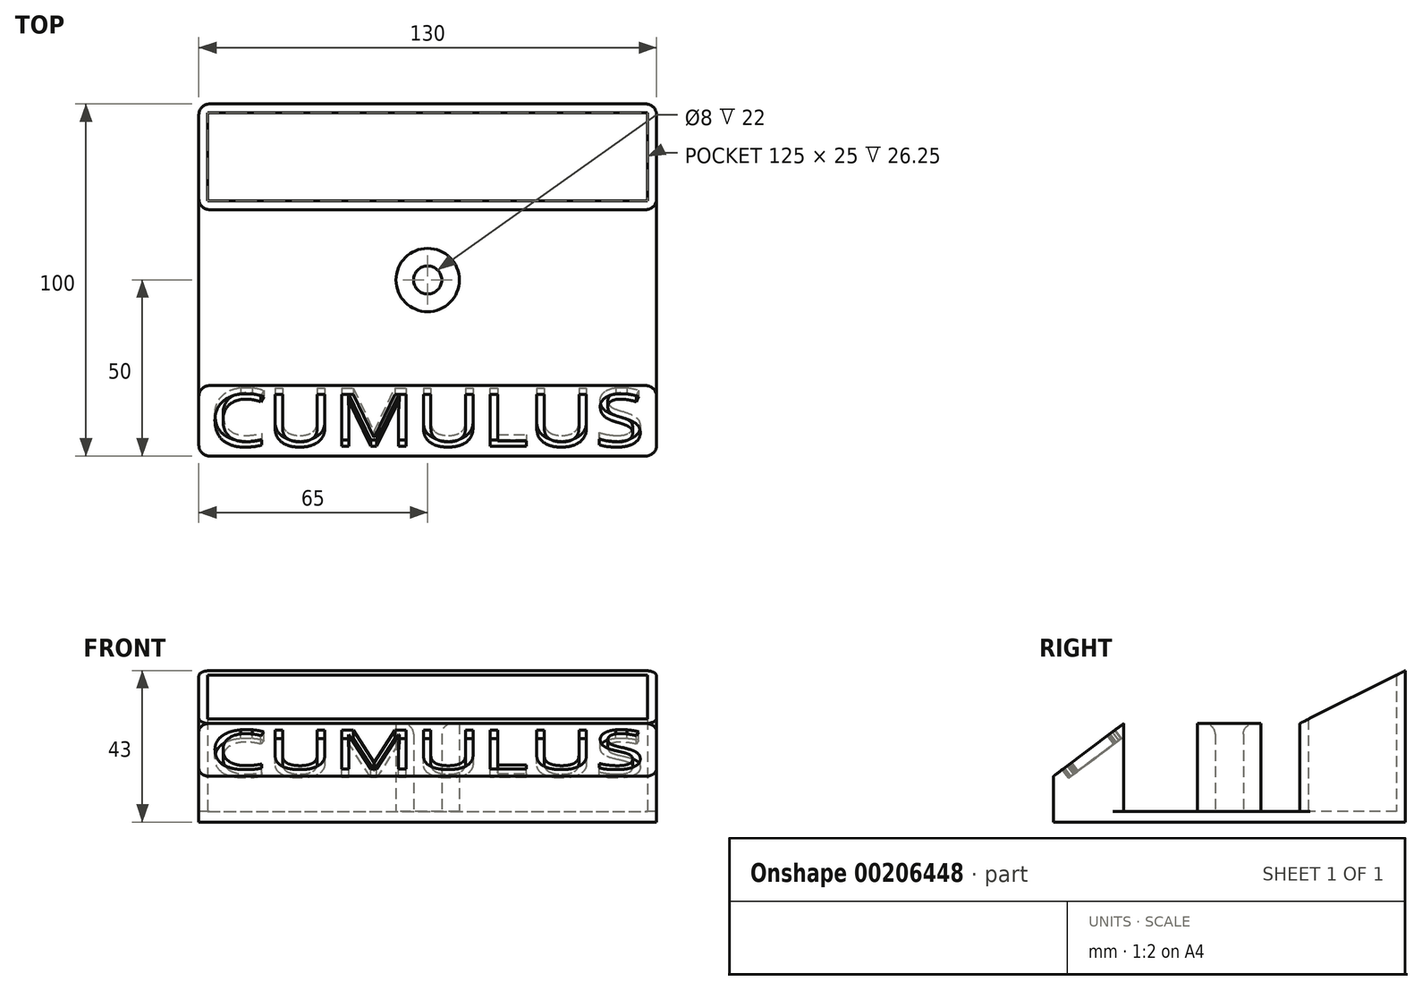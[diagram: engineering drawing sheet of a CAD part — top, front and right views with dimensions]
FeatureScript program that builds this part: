
annotation { "Feature Type Name" : "Feature", "Feature Type Description" : "" }
export const myFeature = defineFeature(function(context is Context, id is Id, definition is map)
    precondition{}
    {
        {
            var Q0;
            Q0=qCreatedBy(makeId("Top.planeOp"),FACE);
            var sketch = newSketch(context, id + "F0", { "sketchPlane" : qUnion([Q0])});
            skLineSegment(sketch, "E0.bottom", {"start": v(-65, 100) * mm, "end": v(65, 100) * mm});
            skLineSegment(sketch, "E0.top", {"start": v(-65, 0) * mm, "end": v(65, 0) * mm});
            skLineSegment(sketch, "E0.left", {"start": v(65, 100) * mm, "end": v(65, 0) * mm});
            skLineSegment(sketch, "E0.right", {"start": v(-65, 100) * mm, "end": v(-65, 0) * mm});
            skSolve(sketch);
        }
        {
            var Q0;
            Q0=makeQuery(id+"F0.imprint","IMPRINT",FACE,{"disambiguationData":[TD([[makeQuery(id+"F0.imprint","IMPRINT",EDGE,{"derivedFrom":sQuery(id+"F0.wireOp",EDGE,"E0.bottom")}),-1.0]])]});
            extrude(context, id + "F1", {"entities" : qUnion([Q0]), "depth" : 3 * mm});
        }
        {
            var Q0;
            Q0=makeQuery(id+"F1.opExtrude","CAP_FACE",FACE,{"disambiguationData":[OSD([sQuery(id+"F0.wireOp",EDGE,"E0.bottom"),sQuery(id+"F0.wireOp",EDGE,"E0.top"),sQuery(id+"F0.wireOp",EDGE,"E0.left"),sQuery(id+"F0.wireOp",EDGE,"E0.right")])],"isStart":false});
            var sketch = newSketch(context, id + "F2", { "sketchPlane" : qUnion([Q0])});
            skLineSegment(sketch, "E1", {"start": v(0, 0) * mm, "end": v(0, 100) * mm, "construction": true});
            skCircle(sketch, "E2", {"center": v(0, 50) * mm, "radius": 9 * mm});
            skCircle(sketch, "E3", {"center": v(0, 50) * mm, "radius": 4 * mm});
            skLineSegment(sketch, "E4.bottom", {"start": v(-65, 0) * mm, "end": v(65, 0) * mm});
            skLineSegment(sketch, "E4.top", {"start": v(-65, 20) * mm, "end": v(65, 20) * mm});
            skLineSegment(sketch, "E4.left", {"start": v(-65, 0) * mm, "end": v(-65, 20) * mm});
            skLineSegment(sketch, "E4.right", {"start": v(65, 0) * mm, "end": v(65, 20) * mm});
            skLineSegment(sketch, "E5.bottom", {"start": v(-65, 100) * mm, "end": v(65, 100) * mm});
            skLineSegment(sketch, "E5.top", {"start": v(-65, 70) * mm, "end": v(65, 70) * mm});
            skLineSegment(sketch, "E5.left", {"start": v(-65, 100) * mm, "end": v(-65, 70) * mm});
            skLineSegment(sketch, "E5.right", {"start": v(65, 100) * mm, "end": v(65, 70) * mm});
            skLineSegment(sketch, "E6.0", {"start": v(62.5, 97.5) * mm, "end": v(62.5, 72.5) * mm});
            skLineSegment(sketch, "E6.1", {"start": v(-62.5, 97.5) * mm, "end": v(62.5, 97.5) * mm});
            skLineSegment(sketch, "E6.2", {"start": v(-62.5, 97.5) * mm, "end": v(-62.5, 72.5) * mm});
            skLineSegment(sketch, "E6.3", {"start": v(-62.5, 72.5) * mm, "end": v(62.5, 72.5) * mm});
            skSolve(sketch);
        }
        {
            var Q0;
            Q0=makeQuery(id+"F2.imprint","IMPRINT",FACE,{"disambiguationData":[TD([[makeQuery(id+"F2.imprint","IMPRINT",EDGE,{"derivedFrom":sQuery(id+"F2.wireOp",EDGE,"E5.bottom")}),-1.0]])]});
            extrude(context, id + "F3", {"entities" : qUnion([Q0]), "operationType" : NewBodyOperationType.ADD, "depth" : 40 * mm});
        }
        {
            var Q0;
            Q0=makeQuery(id+"F2.imprint","IMPRINT",FACE,{"disambiguationData":[TD([[makeQuery(id+"F2.imprint","IMPRINT",EDGE,{"derivedFrom":sQuery(id+"F2.wireOp",EDGE,"E2")}),1.0]])]});
            var Q1;
            Q1=makeQuery(id+"F2.imprint","IMPRINT",FACE,{"disambiguationData":[TD([[makeQuery(id+"F2.imprint","IMPRINT",EDGE,{"derivedFrom":sQuery(id+"F2.wireOp",EDGE,"E4.bottom")}),1.0]])]});
            extrude(context, id + "F4", {"entities" : qUnion([Q0, Q1]), "operationType" : NewBodyOperationType.ADD, "depth" : 25 * mm});
        }
        {
            var Q0;
            Q0=makeQuery(id+"F4.opExtrude","CAP_EDGE",EDGE,{"disambiguationData":[OSD([sQuery(id+"F2.wireOp",EDGE,"E4.bottom")])],"isStart":false});
            chamfer(context, id + "F5", {"entities" : qUnion([Q0]), "chamferType" : ChamferType.TWO_OFFSETS, "width1" : 20 * mm, "oppositeDirection" : false, "width2" : 15 * mm, "tangentPropagation" : true});
        }
        {
            var Q0;
            Q0=makeQuery(id+"F3.opExtrude","CAP_EDGE",EDGE,{"disambiguationData":[OSD([sQuery(id+"F2.wireOp",EDGE,"E5.top")])],"isStart":false});
            chamfer(context, id + "F6", {"entities" : qUnion([Q0]), "chamferType" : ChamferType.TWO_OFFSETS, "width1" : 30 * mm, "oppositeDirection" : false, "width2" : 15 * mm, "tangentPropagation" : true});
        }
        {
            var Q0;
            Q0=makeQuery(id+"F3.boolean.opBoolean","MERGE",EDGE,{"derivedFrom":[makeQuery(id+"F1.opExtrude","SWEPT_EDGE",EDGE,{"disambiguationData":[OSD([sQuery(id+"F0.wireOp",EDGE,"E0.bottom"),sQuery(id+"F0.wireOp",EDGE,"E0.right")])]}),makeQuery(id+"F3.opExtrude","SWEPT_EDGE",EDGE,{"disambiguationData":[OSD([sQuery(id+"F2.wireOp",EDGE,"E5.bottom"),sQuery(id+"F2.wireOp",EDGE,"E5.left")])]})]});
            var Q1;
            Q1=makeQuery(id+"F3.opExtrude","SWEPT_EDGE",EDGE,{"disambiguationData":[OSD([sQuery(id+"F0.wireOp",EDGE,"E0.right"),sQuery(id+"F2.wireOp",EDGE,"E5.top"),sQuery(id+"F2.wireOp",EDGE,"E5.left")])]});
            var Q2;
            Q2=makeQuery(id+"F3.opExtrude","SWEPT_EDGE",EDGE,{"disambiguationData":[OSD([sQuery(id+"F0.wireOp",EDGE,"E0.left"),sQuery(id+"F2.wireOp",EDGE,"E5.top"),sQuery(id+"F2.wireOp",EDGE,"E5.right")])]});
            var Q3;
            Q3=makeQuery(id+"F4.boolean.opBoolean","MERGE",EDGE,{"derivedFrom":[makeQuery(id+"F1.opExtrude","SWEPT_EDGE",EDGE,{"disambiguationData":[OSD([sQuery(id+"F0.wireOp",EDGE,"E0.top"),sQuery(id+"F0.wireOp",EDGE,"E0.right")])]}),makeQuery(id+"F4.opExtrude","SWEPT_EDGE",EDGE,{"disambiguationData":[OSD([sQuery(id+"F2.wireOp",EDGE,"E4.bottom"),sQuery(id+"F2.wireOp",EDGE,"E4.left")])]})]});
            var Q4;
            Q4=makeQuery(id+"F3.boolean.opBoolean","MERGE",EDGE,{"derivedFrom":[makeQuery(id+"F1.opExtrude","SWEPT_EDGE",EDGE,{"disambiguationData":[OSD([sQuery(id+"F0.wireOp",EDGE,"E0.bottom"),sQuery(id+"F0.wireOp",EDGE,"E0.left")])]}),makeQuery(id+"F3.opExtrude","SWEPT_EDGE",EDGE,{"disambiguationData":[OSD([sQuery(id+"F2.wireOp",EDGE,"E5.bottom"),sQuery(id+"F2.wireOp",EDGE,"E5.right")])]})]});
            var Q5;
            Q5=makeQuery(id+"F4.boolean.opBoolean","MERGE",EDGE,{"derivedFrom":[makeQuery(id+"F1.opExtrude","SWEPT_EDGE",EDGE,{"disambiguationData":[OSD([sQuery(id+"F0.wireOp",EDGE,"E0.top"),sQuery(id+"F0.wireOp",EDGE,"E0.left")])]}),makeQuery(id+"F4.opExtrude","SWEPT_EDGE",EDGE,{"disambiguationData":[OSD([sQuery(id+"F2.wireOp",EDGE,"E4.bottom"),sQuery(id+"F2.wireOp",EDGE,"E4.right")])]})]});
            var Q6;
            Q6=makeQuery(id+"F4.opExtrude","SWEPT_EDGE",EDGE,{"disambiguationData":[OSD([sQuery(id+"F0.wireOp",EDGE,"E0.left"),sQuery(id+"F2.wireOp",EDGE,"E4.top"),sQuery(id+"F2.wireOp",EDGE,"E4.right")])]});
            var Q7;
            Q7=makeQuery(id+"F4.opExtrude","SWEPT_EDGE",EDGE,{"disambiguationData":[OSD([sQuery(id+"F0.wireOp",EDGE,"E0.right"),sQuery(id+"F2.wireOp",EDGE,"E4.top"),sQuery(id+"F2.wireOp",EDGE,"E4.left")])]});
            var Q8;
            Q8=makeQuery(id+"F4.opExtrude","CAP_EDGE",EDGE,{"disambiguationData":[OSD([sQuery(id+"F2.wireOp",EDGE,"E3")])],"isStart":false});
            fillet(context, id + "F7", {"entities" : qUnion([Q0, Q1, Q2, Q3, Q4, Q5, Q6, Q7, Q8]), "radius" : 3 * mm, "tangentPropagation" : true, "allowEdgeOverflow" : false});
        }
        {
            var Q0;
            Q0=makeQuery(id+"F5.opChamfer","BLEND_FACE",FACE,{"disambiguationData":[OSD([sQuery(id+"F2.wireOp",EDGE,"E4.bottom")])]});
            var sketch = newSketch(context, id + "F8", { "sketchPlane" : qUnion([Q0])});
            skLineSegment(sketch, "E7.0", {"start": v(62, 10.8) * mm, "end": v(-62, 10.8) * mm});
            skLineSegment(sketch, "E8.0", {"start": v(-62, 29.8) * mm, "end": v(62, 29.8) * mm});
            skText(sketch, "E9", { "text": "CUMULUS", "fontName": "OpenSans-Regular.ttf"});
            skLineSegment(sketch, "E10", {"start": v(-62, 10.8) * mm, "end": v(-62, 47.82) * mm});
            skLineSegment(sketch, "E11", {"start": v(62, 10.8) * mm, "end": v(62, 49.07) * mm});
            skPoint(sketch, "E11.endSnap0", {"position": v(62, 15.3) * mm});
            const initialGuessF8  = {"E9": [-0.062, 0.0112, 1, 0, 0.0186]};
            skSetInitialGuess(sketch, initialGuessF8);
            skSolve(sketch);
        }
        {
            var Q0;
            Q0=makeQuery(id+"F8.imprint","IMPRINT",FACE,{"disambiguationData":[TD([[makeQuery(id+"F8.imprint","IMPRINT",EDGE,{"derivedFrom":sQuery(id+"F8.wireOp",EDGE,"E9.sketch_text.stroke-0")}),-1.0]])]});
            var Q1;
            Q1=makeQuery(id+"F8.imprint","IMPRINT",FACE,{"disambiguationData":[TD([[makeQuery(id+"F8.imprint","IMPRINT",EDGE,{"derivedFrom":sQuery(id+"F8.wireOp",EDGE,"E9.sketch_text.stroke-13")}),-1.0]])]});
            var Q2;
            Q2=makeQuery(id+"F8.imprint","IMPRINT",FACE,{"disambiguationData":[TD([[makeQuery(id+"F8.imprint","IMPRINT",EDGE,{"derivedFrom":sQuery(id+"F8.wireOp",EDGE,"E9.sketch_text.stroke-19")}),-1.0]])]});
            var Q3;
            Q3=makeQuery(id+"F8.imprint","IMPRINT",FACE,{"disambiguationData":[TD([[makeQuery(id+"F8.imprint","IMPRINT",EDGE,{"derivedFrom":sQuery(id+"F8.wireOp",EDGE,"E9.sketch_text.stroke-27")}),-1.0]])]});
            var Q4;
            Q4=makeQuery(id+"F8.imprint","IMPRINT",FACE,{"disambiguationData":[TD([[makeQuery(id+"F8.imprint","IMPRINT",EDGE,{"derivedFrom":sQuery(id+"F8.wireOp",EDGE,"E9.sketch_text.stroke-43")}),-1.0]])]});
            var Q5;
            Q5=makeQuery(id+"F8.imprint","IMPRINT",FACE,{"disambiguationData":[TD([[makeQuery(id+"F8.imprint","IMPRINT",EDGE,{"derivedFrom":sQuery(id+"F8.wireOp",EDGE,"E9.sketch_text.stroke-58")}),-1.0]])]});
            var Q6;
            Q6=makeQuery(id+"F8.imprint","IMPRINT",FACE,{"disambiguationData":[TD([[makeQuery(id+"F8.imprint","IMPRINT",EDGE,{"derivedFrom":sQuery(id+"F8.wireOp",EDGE,"E9.sketch_text.stroke-72")}),-1.0]])]});
            var Q7;
            Q7=makeQuery(id+"F8.imprint","IMPRINT",FACE,{"disambiguationData":[TD([[makeQuery(id+"F8.imprint","IMPRINT",EDGE,{"derivedFrom":sQuery(id+"F8.wireOp",EDGE,"E9.sketch_text.stroke-90")}),-1.0]])]});
            var Q8;
            Q8=makeQuery(id+"F8.imprint","IMPRINT",FACE,{"disambiguationData":[TD([[makeQuery(id+"F8.imprint","IMPRINT",EDGE,{"derivedFrom":sQuery(id+"F8.wireOp",EDGE,"E9.sketch_text.stroke-104")}),-1.0]])]});
            var Q9;
            Q9=makeQuery(id+"F8.imprint","IMPRINT",FACE,{"disambiguationData":[TD([[makeQuery(id+"F8.imprint","IMPRINT",EDGE,{"derivedFrom":sQuery(id+"F8.wireOp",EDGE,"E9.sketch_text.stroke-61")}),-1.0]])]});
            extrude(context, id + "F9", {"entities" : qUnion([Q0, Q1, Q2, Q3, Q4, Q5, Q6, Q7, Q8, Q9]), "operationType" : NewBodyOperationType.REMOVE, "oppositeDirection" : true, "depth" : 3 * mm});
        }
    });
